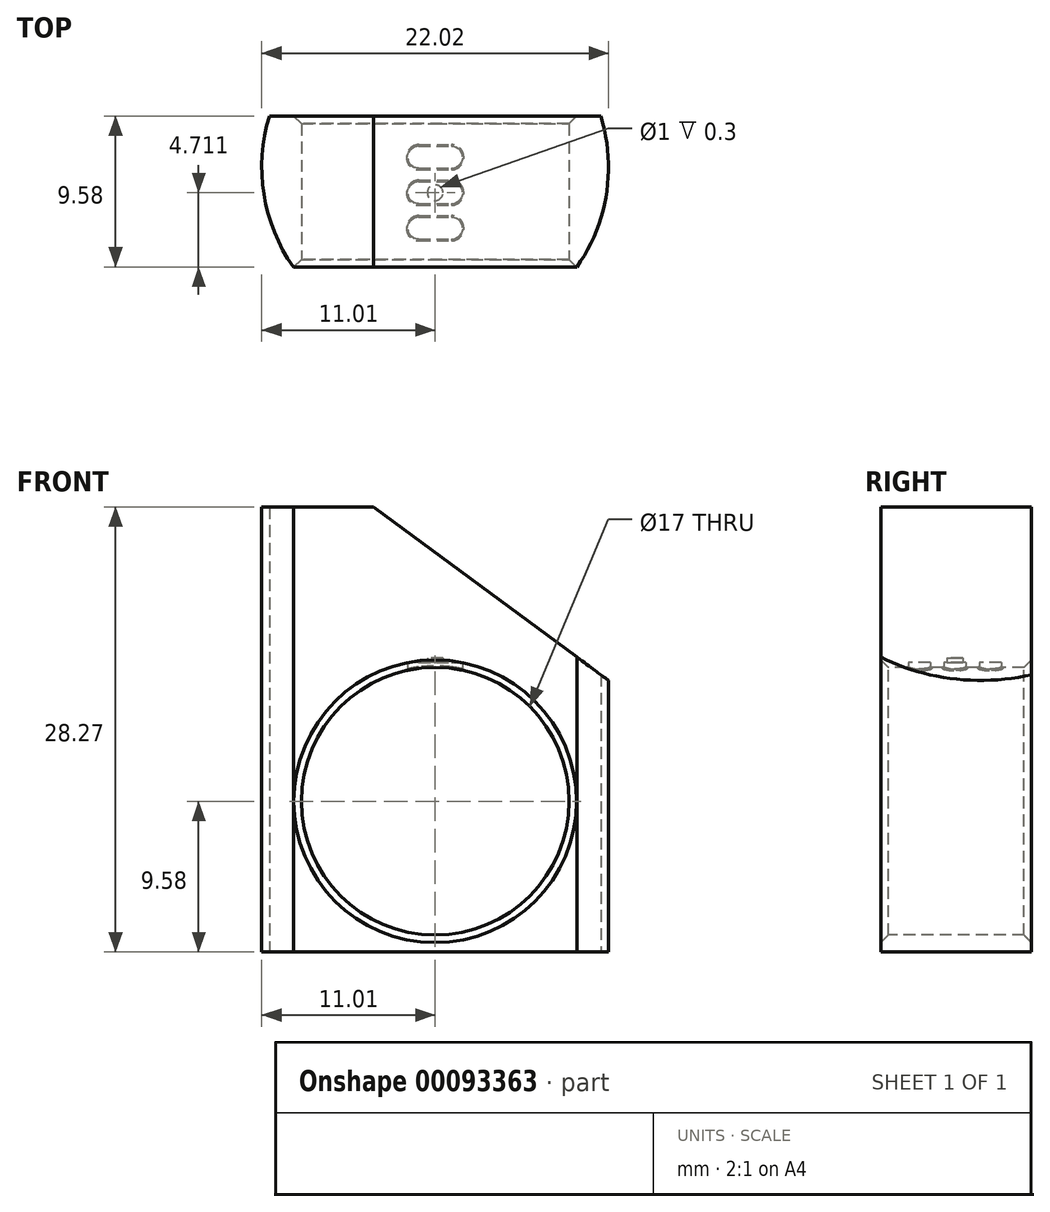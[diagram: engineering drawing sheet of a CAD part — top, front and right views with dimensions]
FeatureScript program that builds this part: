
annotation { "Feature Type Name" : "Feature", "Feature Type Description" : "" }
export const myFeature = defineFeature(function(context is Context, id is Id, definition is map)
    precondition{}
    {
        {
            var Q0;
            Q0=qCreatedBy(makeId("Front.planeOp"),FACE);
            var sketch = newSketch(context, id + "F0", { "sketchPlane" : qUnion([Q0])});
            skCircle(sketch, "E0", {"center": v(0, 0) * mm, "radius": 8.88 * mm});
            skSolve(sketch);
        }
        {
            var Q0;
            Q0=qCreatedBy(makeId("Top.planeOp"),FACE);
            var sketch = newSketch(context, id + "F1", { "sketchPlane" : qUnion([Q0])});
            skCircle(sketch, "E1", {"center": v(0, 0) * mm, "radius": 11.5 * mm});
            skSolve(sketch);
        }
        {
            var Q0;
            Q0=qSketchRegion(id+"F1",true);
            extrude(context, id + "F2", {"entities" : qUnion([Q0]), "depth" : 19.52 * mm, "hasSecondDirection" : true, "secondDirectionOppositeDirection" : true, "secondDirectionDepth" : 10 * mm});
        }
        {
            var Q0;
            Q0=qSketchRegion(id+"F0",true);
            extrude(context, id + "F3", {"entities" : qUnion([Q0]), "operationType" : NewBodyOperationType.REMOVE, "oppositeDirection" : true, "depth" : 25 * mm, "hasSecondDirection" : true, "secondDirectionOppositeDirection" : false, "secondDirectionDepth" : 25 * mm});
        }
        {
            var Q0;
            Q0=qCreatedBy(makeId("Front.planeOp"),FACE);
            var sketch = newSketch(context, id + "F4", { "sketchPlane" : qUnion([Q0])});
            skLineSegment(sketch, "E2", {"start": v(-16.33, 28.55) * mm, "end": v(24.77, -1.78) * mm});
            skLineSegment(sketch, "E3", {"start": v(24.77, -1.78) * mm, "end": v(24.77, 28.55) * mm});
            skLineSegment(sketch, "E4", {"start": v(24.77, 28.55) * mm, "end": v(-16.33, 28.55) * mm});
            skSolve(sketch);
        }
        {
            var Q0;
            Q0=qSketchRegion(id+"F4",true);
            extrude(context, id + "F5", {"entities" : qUnion([Q0]), "operationType" : NewBodyOperationType.REMOVE, "oppositeDirection" : true, "depth" : 25 * mm, "hasSecondDirection" : true, "secondDirectionOppositeDirection" : false, "secondDirectionDepth" : 25 * mm});
        }
        {
            var Q0;
            Q0=qCreatedBy(makeId("Top.planeOp"),FACE);
            var sketch = newSketch(context, id + "F6", { "sketchPlane" : qUnion([Q0])});
            skLineSegment(sketch, "E5.bottom", {"start": v(-13.62, -6.62) * mm, "end": v(17.44, -6.62) * mm});
            skLineSegment(sketch, "E5.top", {"start": v(-13.62, 3.38) * mm, "end": v(17.44, 3.38) * mm});
            skLineSegment(sketch, "E5.left", {"start": v(-13.62, -6.62) * mm, "end": v(-13.62, 3.38) * mm});
            skLineSegment(sketch, "E5.right", {"start": v(17.44, -6.62) * mm, "end": v(17.44, 3.38) * mm});
            skLineSegment(sketch, "E6", {"start": v(-13.62, 3.38) * mm, "end": v(-13.62, 17.25) * mm});
            skLineSegment(sketch, "E7", {"start": v(-13.62, 17.25) * mm, "end": v(17.44, 17.25) * mm});
            skLineSegment(sketch, "E8", {"start": v(17.44, 17.25) * mm, "end": v(17.44, 3.38) * mm});
            skLineSegment(sketch, "E9", {"start": v(-13.62, -6.62) * mm, "end": v(-13.62, -19.8) * mm});
            skLineSegment(sketch, "E10", {"start": v(-13.62, -19.8) * mm, "end": v(17.44, -19.8) * mm});
            skLineSegment(sketch, "E11", {"start": v(17.44, -19.8) * mm, "end": v(17.44, -6.62) * mm});
            skSolve(sketch);
        }
        {
            var Q0;
            Q0=makeQuery(id+"F6.imprint","IMPRINT",FACE,{"disambiguationData":[TD([[makeQuery(id+"F6.imprint","IMPRINT",EDGE,{"derivedFrom":sQuery(id+"F6.wireOp",EDGE,"E5.top")}),1.0]])]});
            var Q1;
            Q1=makeQuery(id+"F6.imprint","IMPRINT",FACE,{"disambiguationData":[TD([[makeQuery(id+"F6.imprint","IMPRINT",EDGE,{"derivedFrom":sQuery(id+"F6.wireOp",EDGE,"E5.bottom")}),-1.0]])]});
            extrude(context, id + "F7", {"entities" : qUnion([Q0, Q1]), "operationType" : NewBodyOperationType.REMOVE, "oppositeDirection" : true, "depth" : 25 * mm, "hasSecondDirection" : true, "secondDirectionOppositeDirection" : false, "secondDirectionDepth" : 25 * mm});
        }
        {
            var Q0;
            Q0=makeQuery(id+"F7.boolean.opBoolean","INTERSECT",EDGE,{"derivedFrom":[makeQuery(id+"F3.boolean.opBoolean","COPY",FACE,{"derivedFrom":makeQuery(id+"F3.opExtrude","SWEPT_FACE",FACE,{"disambiguationData":[OSD([sQuery(id+"F0.wireOp",EDGE,"E0")])]})}),makeQuery(id+"F7.opExtrude","SWEPT_FACE",FACE,{"disambiguationData":[OSD([sQuery(id+"F6.wireOp",EDGE,"E5.top")])]})]});
            var Q1;
            Q1=makeQuery(id+"F7.boolean.opBoolean","INTERSECT",EDGE,{"derivedFrom":[makeQuery(id+"F3.boolean.opBoolean","COPY",FACE,{"derivedFrom":makeQuery(id+"F3.opExtrude","SWEPT_FACE",FACE,{"disambiguationData":[OSD([sQuery(id+"F0.wireOp",EDGE,"E0")])]})}),makeQuery(id+"F7.opExtrude","SWEPT_FACE",FACE,{"disambiguationData":[OSD([sQuery(id+"F6.wireOp",EDGE,"E5.bottom")])]})]});
            chamfer(context, id + "F8", {"entities" : qUnion([Q0, Q1]), "width" : .5 * mm, "tangentPropagation" : true});
        }
        {
            var Q0;
            Q0=makeQuery(id+"F2.opExtrude","SWEPT_BODY",BODY,{"disambiguationData":[OSD([sQuery(id+"F1.wireOp",EDGE,"E1")])]});
            var Q1;
            Q1=qCreatedBy(makeId("Origin.pointOp"),VERTEX);
            transform(context, id + "F9", {"entities" : qUnion([Q0]), "transformType" : TransformType.SCALE_UNIFORMLY, "scale" : 0.96, "scalePoint" : qUnion([Q1]), "makeCopy" : false});
        }
        {
            var Q0;
            Q0=qCreatedBy(makeId("Top.planeOp"),FACE);
            var sketch = newSketch(context, id + "F10", { "sketchPlane" : qUnion([Q0])});
            skPoint(sketch, "E12", {"position": v(0, -11.67) * mm});
            skLineSegment(sketch, "E13.bottom", {"start": v(-1.05, -2.33) * mm, "end": v(1.04, -2.33) * mm});
            skArc(sketch, "E14.filletArc", {"start": v(-1.05, -0.93) * mm, "mid": v(-1.55, -1.13) * mm, "end": v(-1.75, -1.63) * mm});
            skArc(sketch, "E15.filletArc", {"start": v(-1.75, -1.63) * mm, "mid": v(-1.55, -2.12) * mm, "end": v(-1.05, -2.33) * mm});
            skArc(sketch, "E16.filletArc", {"start": v(1.74, -1.63) * mm, "mid": v(1.54, -1.13) * mm, "end": v(1.04, -0.93) * mm});
            skArc(sketch, "E17.filletArc", {"start": v(1.04, -2.33) * mm, "mid": v(1.54, -2.12) * mm, "end": v(1.74, -1.63) * mm});
            skLineSegment(sketch, "E18.bottom", {"start": v(-1.05, -4.58) * mm, "end": v(1.04, -4.58) * mm});
            skLineSegment(sketch, "E18.top", {"start": v(-1.05, -3.18) * mm, "end": v(1.04, -3.18) * mm});
            skArc(sketch, "E19.filletArc", {"start": v(-1.05, -3.18) * mm, "mid": v(-1.55, -3.39) * mm, "end": v(-1.75, -3.88) * mm});
            skArc(sketch, "E20.filletArc", {"start": v(-1.75, -3.88) * mm, "mid": v(-1.55, -4.38) * mm, "end": v(-1.05, -4.58) * mm});
            skArc(sketch, "E21.filletArc", {"start": v(1.74, -3.88) * mm, "mid": v(1.54, -3.39) * mm, "end": v(1.04, -3.18) * mm});
            skArc(sketch, "E22.filletArc", {"start": v(1.04, -4.58) * mm, "mid": v(1.54, -4.38) * mm, "end": v(1.74, -3.88) * mm});
            skLineSegment(sketch, "E23", {"start": v(-1.05, -0.93) * mm, "end": v(1.04, -0.93) * mm});
            skCircle(sketch, "E24", {"center": v(0, -1.63) * mm, "radius": 0.5 * mm});
            skLineSegment(sketch, "E25.bottom", {"start": v(-1.05, -0.07) * mm, "end": v(1.04, -0.07) * mm});
            skLineSegment(sketch, "E25.top", {"start": v(-1.05, 1.33) * mm, "end": v(1.04, 1.33) * mm});
            skArc(sketch, "E26.filletArc", {"start": v(-1.05, 1.33) * mm, "mid": v(-1.55, 1.12) * mm, "end": v(-1.75, 0.63) * mm});
            skArc(sketch, "E27.filletArc", {"start": v(-1.75, 0.63) * mm, "mid": v(-1.55, 0.13) * mm, "end": v(-1.05, -0.07) * mm});
            skArc(sketch, "E28.filletArc", {"start": v(1.74, 0.63) * mm, "mid": v(1.54, 1.12) * mm, "end": v(1.04, 1.33) * mm});
            skArc(sketch, "E29.filletArc", {"start": v(1.04, -0.07) * mm, "mid": v(1.54, 0.13) * mm, "end": v(1.74, 0.63) * mm});
            skSolve(sketch);
        }
        {
            var Q0;
            Q0=makeQuery(id+"F10.imprint","IMPRINT",FACE,{"disambiguationData":[TD([[makeQuery(id+"F10.imprint","IMPRINT",EDGE,{"derivedFrom":sQuery(id+"F10.wireOp",EDGE,"E18.bottom")}),1.0]])]});
            var Q1;
            Q1=makeQuery(id+"F10.imprint","IMPRINT",FACE,{"disambiguationData":[TD([[makeQuery(id+"F10.imprint","IMPRINT",EDGE,{"derivedFrom":sQuery(id+"F10.wireOp",EDGE,"E25.bottom")}),1.0]])]});
            var Q2;
            Q2=makeQuery(id+"F10.imprint","IMPRINT",FACE,{"disambiguationData":[TD([[makeQuery(id+"F10.imprint","IMPRINT",EDGE,{"derivedFrom":sQuery(id+"F10.wireOp",EDGE,"E13.bottom")}),1.0]])]});
            extrude(context, id + "F11", {"entities" : qUnion([Q0, Q1, Q2]), "operationType" : NewBodyOperationType.REMOVE, "depth" : ((17 / 2) + .3) * mm});
        }
        {
            var Q0;
            Q0=makeQuery(id+"F11.boolean.opBoolean","INTERSECT",EDGE,{"derivedFrom":[makeQuery(id+"F3.boolean.opBoolean","COPY",FACE,{"derivedFrom":makeQuery(id+"F3.opExtrude","SWEPT_FACE",FACE,{"disambiguationData":[OSD([sQuery(id+"F0.wireOp",EDGE,"E0")])]})}),makeQuery(id+"F11.opExtrude","SWEPT_FACE",FACE,{"disambiguationData":[OSD([sQuery(id+"F10.wireOp",EDGE,"E25.top")])]})]});
            var Q1;
            Q1=makeQuery(id+"F11.boolean.opBoolean","INTERSECT",EDGE,{"derivedFrom":[makeQuery(id+"F3.boolean.opBoolean","COPY",FACE,{"derivedFrom":makeQuery(id+"F3.opExtrude","SWEPT_FACE",FACE,{"disambiguationData":[OSD([sQuery(id+"F0.wireOp",EDGE,"E0")])]})}),makeQuery(id+"F11.opExtrude","SWEPT_FACE",FACE,{"disambiguationData":[OSD([sQuery(id+"F10.wireOp",EDGE,"E28.filletArc"),sQuery(id+"F10.wireOp",EDGE,"E29.filletArc")])]})]});
            var Q2;
            Q2=makeQuery(id+"F11.boolean.opBoolean","INTERSECT",EDGE,{"derivedFrom":[makeQuery(id+"F3.boolean.opBoolean","COPY",FACE,{"derivedFrom":makeQuery(id+"F3.opExtrude","SWEPT_FACE",FACE,{"disambiguationData":[OSD([sQuery(id+"F0.wireOp",EDGE,"E0")])]})}),makeQuery(id+"F11.opExtrude","SWEPT_FACE",FACE,{"disambiguationData":[OSD([sQuery(id+"F10.wireOp",EDGE,"E26.filletArc"),sQuery(id+"F10.wireOp",EDGE,"E27.filletArc")])]})]});
            var Q3;
            Q3=makeQuery(id+"F11.boolean.opBoolean","INTERSECT",EDGE,{"derivedFrom":[makeQuery(id+"F3.boolean.opBoolean","COPY",FACE,{"derivedFrom":makeQuery(id+"F3.opExtrude","SWEPT_FACE",FACE,{"disambiguationData":[OSD([sQuery(id+"F0.wireOp",EDGE,"E0")])]})}),makeQuery(id+"F11.opExtrude","SWEPT_FACE",FACE,{"disambiguationData":[OSD([sQuery(id+"F10.wireOp",EDGE,"E25.bottom")])]})]});
            var Q4;
            Q4=makeQuery(id+"F11.boolean.opBoolean","INTERSECT",EDGE,{"derivedFrom":[makeQuery(id+"F3.boolean.opBoolean","COPY",FACE,{"derivedFrom":makeQuery(id+"F3.opExtrude","SWEPT_FACE",FACE,{"disambiguationData":[OSD([sQuery(id+"F0.wireOp",EDGE,"E0")])]})}),makeQuery(id+"F11.opExtrude","SWEPT_FACE",FACE,{"disambiguationData":[OSD([sQuery(id+"F10.wireOp",EDGE,"E18.top")])]})]});
            var Q5;
            Q5=makeQuery(id+"F11.boolean.opBoolean","INTERSECT",EDGE,{"derivedFrom":[makeQuery(id+"F3.boolean.opBoolean","COPY",FACE,{"derivedFrom":makeQuery(id+"F3.opExtrude","SWEPT_FACE",FACE,{"disambiguationData":[OSD([sQuery(id+"F0.wireOp",EDGE,"E0")])]})}),makeQuery(id+"F11.opExtrude","SWEPT_FACE",FACE,{"disambiguationData":[OSD([sQuery(id+"F10.wireOp",EDGE,"E19.filletArc"),sQuery(id+"F10.wireOp",EDGE,"E20.filletArc")])]})]});
            var Q6;
            Q6=makeQuery(id+"F11.boolean.opBoolean","INTERSECT",EDGE,{"derivedFrom":[makeQuery(id+"F3.boolean.opBoolean","COPY",FACE,{"derivedFrom":makeQuery(id+"F3.opExtrude","SWEPT_FACE",FACE,{"disambiguationData":[OSD([sQuery(id+"F0.wireOp",EDGE,"E0")])]})}),makeQuery(id+"F11.opExtrude","SWEPT_FACE",FACE,{"disambiguationData":[OSD([sQuery(id+"F10.wireOp",EDGE,"E18.bottom")])]})]});
            var Q7;
            Q7=makeQuery(id+"F11.boolean.opBoolean","INTERSECT",EDGE,{"derivedFrom":[makeQuery(id+"F3.boolean.opBoolean","COPY",FACE,{"derivedFrom":makeQuery(id+"F3.opExtrude","SWEPT_FACE",FACE,{"disambiguationData":[OSD([sQuery(id+"F0.wireOp",EDGE,"E0")])]})}),makeQuery(id+"F11.opExtrude","SWEPT_FACE",FACE,{"disambiguationData":[OSD([sQuery(id+"F10.wireOp",EDGE,"E21.filletArc"),sQuery(id+"F10.wireOp",EDGE,"E22.filletArc")])]})]});
            var Q8;
            Q8=makeQuery(id+"F11.boolean.opBoolean","INTERSECT",EDGE,{"derivedFrom":[makeQuery(id+"F3.boolean.opBoolean","COPY",FACE,{"derivedFrom":makeQuery(id+"F3.opExtrude","SWEPT_FACE",FACE,{"disambiguationData":[OSD([sQuery(id+"F0.wireOp",EDGE,"E0")])]})}),makeQuery(id+"F11.opExtrude","SWEPT_FACE",FACE,{"disambiguationData":[OSD([sQuery(id+"F10.wireOp",EDGE,"E16.filletArc"),sQuery(id+"F10.wireOp",EDGE,"E17.filletArc")])]})]});
            var Q9;
            Q9=makeQuery(id+"F11.boolean.opBoolean","INTERSECT",EDGE,{"derivedFrom":[makeQuery(id+"F3.boolean.opBoolean","COPY",FACE,{"derivedFrom":makeQuery(id+"F3.opExtrude","SWEPT_FACE",FACE,{"disambiguationData":[OSD([sQuery(id+"F0.wireOp",EDGE,"E0")])]})}),makeQuery(id+"F11.opExtrude","SWEPT_FACE",FACE,{"disambiguationData":[OSD([sQuery(id+"F10.wireOp",EDGE,"E23")])]})]});
            chamfer(context, id + "F12", {"entities" : qUnion([Q0, Q1, Q2, Q3, Q4, Q5, Q6, Q7, Q8, Q9]), "width" : .1 * mm, "tangentPropagation" : true});
        }
        {
            var Q0;
            Q0=makeQuery(id+"F10.imprint","IMPRINT",FACE,{"disambiguationData":[TD([[makeQuery(id+"F10.imprint","IMPRINT",EDGE,{"derivedFrom":sQuery(id+"F10.wireOp",EDGE,"E24")}),1.0]])]});
            extrude(context, id + "F13", {"entities" : qUnion([Q0]), "operationType" : NewBodyOperationType.REMOVE, "depth" : ((17 / 2) + .6) * mm});
        }
    });
